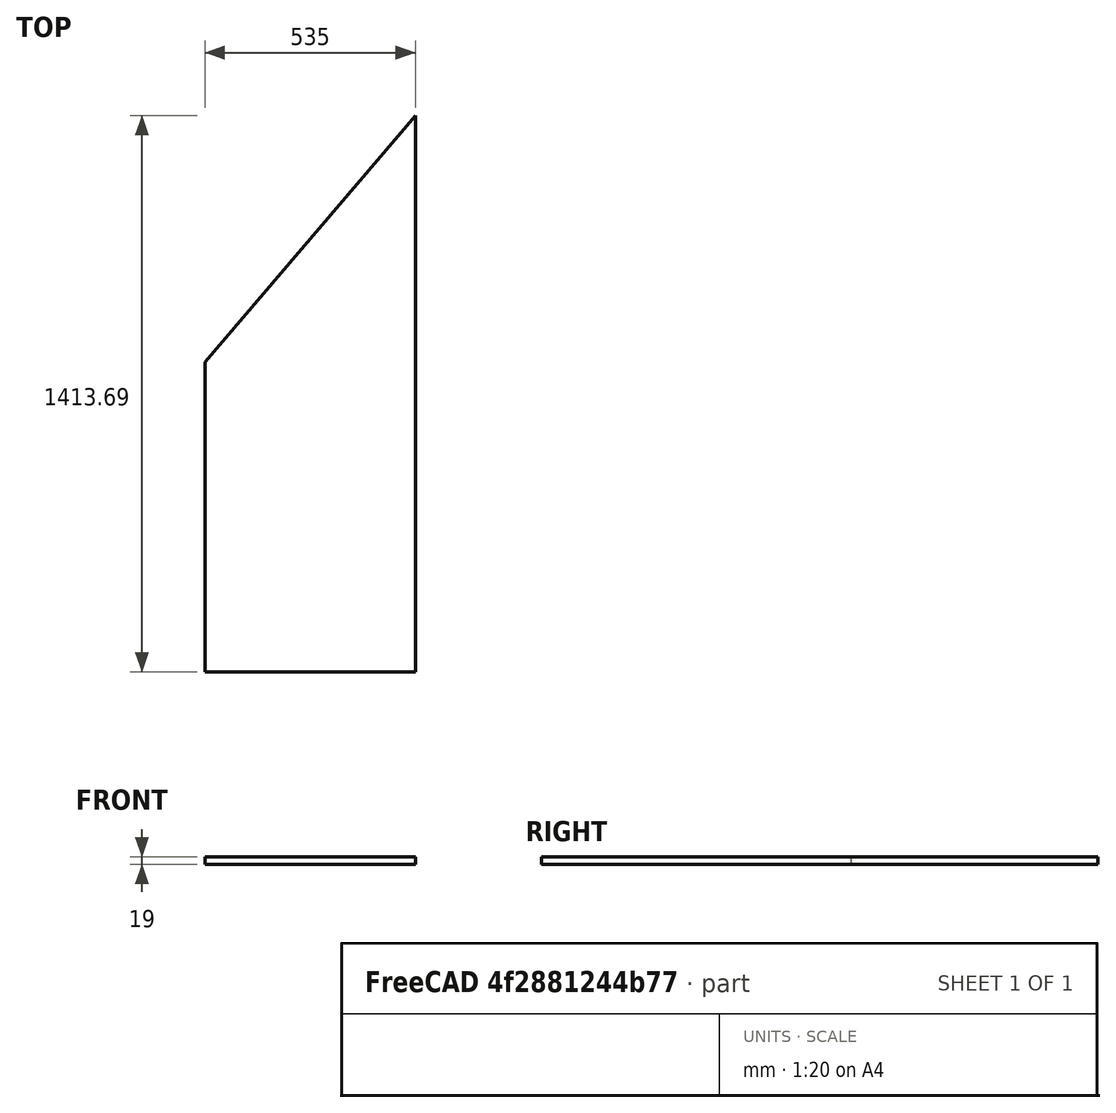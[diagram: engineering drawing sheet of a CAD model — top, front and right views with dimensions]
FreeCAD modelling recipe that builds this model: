
FCSTD DOCUMENT  (FreeCAD 1.0R39285 (Git))
Label: wardrobe_door_corpus02_jan
License: All rights reserved
LicenseURL: https://en.wikipedia.org/wiki/All_rights_reserved
objects: TechDraw::DrawViewDimension×5, PartDesign::CoordinateSystem×2, TechDraw::DrawProjGroupItem×2, Sketcher::SketchObject×1, PartDesign::Pad×1, PartDesign::Body×1, TechDraw::DrawSVGTemplate×1, TechDraw::DrawViewAnnotation×1, TechDraw::DrawPage×1, App::Part×1
note: 15 computed .brp shape members not serialized (recipe doc carries the construction recipe); baked Part::Feature solids carry a one-line shape summary decoded from their .brp
EXTERNAL_REF file=../../mastersheet.FCStd obj=Spreadsheet
EXTERNAL_REF file=../../mastersketch.FCStd obj=Sketch

FEATURE [Sketcher::SketchObject] Sketch
  ArcFitTolerance = 1e-06
  AttachmentSupport = -> [XY_Plane]
  FullyConstrained = true
  MakeInternals = false
  MapMode = 5
  expr: Constraints[0] = mastersketch#Sketch.Constraints.corpus02_door_height
  expr: Constraints[10] = mastersketch#Sketch.Constraints.alpha
  expr: Constraints[3] = mastersheet#Spreadsheet.corpus_width - 5
  sketch-geometry (4):
    g0: LineSegment StartX=0 StartY=0 StartZ=0 EndX=0 EndY=1413.69 EndZ=0
    g1: LineSegment StartX=0 StartY=0 StartZ=0 EndX=-535 EndY=0 EndZ=0
    g2: LineSegment StartX=-535 StartY=0 StartZ=0 EndX=-535 EndY=787.688 EndZ=0
    g3: LineSegment StartX=-535 StartY=787.688 StartZ=0 EndX=0 EndY=1413.69 EndZ=0
  constraints (11):
    c: Distance(g0) = 1413.69
    c: Coincident(g0,g-1)
    c: Vertical(g0)
    c: Distance(g1) = 535
    c: Coincident(g1,g0)
    c: PointOnObject(g1,g-1)
    c: Vertical(g2)
    c: Coincident(g3,g2)
    c: Coincident(g2,g1)
    c: Coincident(g3,g0)
    c: Angle(g2,g3) = 2.43442
FEATURE [PartDesign::Pad] Pad
  Direction = (0,0,1)
  Length = 19
  Length2 = 10
  Profile = -> Sketch
  ReferenceAxis = -> Sketch [N_Axis]
  Refine = true
  Suppressed = false
  Type = 0
FEATURE [PartDesign::Body] Body  label="wardrobe_door_corpus02_jan"
  AllowCompound = false
  Group = -> [Sketch,Pad]
  Origin = -> Origin
  Tip = -> Pad
FEATURE [PartDesign::CoordinateSystem] LCS_1
  AttacherType = Attacher::AttachEngine3D
  AttachmentSupport = -> [Pad]
  MapMode = 7
  Placement = pos=(0,0,0) rot=(1,0,0;1.5708rad)
FEATURE [TechDraw::DrawSVGTemplate] Template  label="Vorlage"
  Height = 210
  Orientation = 1
  Template = <userpath>/scoop/apps/freecad/current/data/Mod/TechDraw/Templates/A4_Landscape_TD.svg
  Width = 297
FEATURE [TechDraw::DrawProjGroupItem] View
  CoarseView = false
  Direction = (0,1e-16,-1)
  Focus = 100
  HardHidden = false
  IsoCount = 0
  IsoHidden = false
  IsoVisible = false
  LockPosition = false
  Perspective = false
  Rotation = 0
  RotationVector = (1,0,0)
  Scale = 0.1
  ScaleType = 2
  ScrubCount = 1
  SeamHidden = false
  SeamVisible = false
  SmoothHidden = false
  SmoothVisible = true
  Source = -> [Body]
  Type = 0
  X = 139.755
  XDirection = (-1e-16,-1,-1e-16)
  Y = 148.199
FEATURE [TechDraw::DrawProjGroupItem] View001
  CoarseView = false
  Direction = (-1,-1e-16,0)
  Focus = 100
  HardHidden = false
  IsoCount = 0
  IsoHidden = false
  IsoVisible = false
  LockPosition = false
  Perspective = false
  Rotation = 0
  RotationVector = (1,0,0)
  Scale = 0.1
  ScaleType = 2
  ScrubCount = 1
  SeamHidden = false
  SeamVisible = false
  SmoothHidden = false
  SmoothVisible = true
  Source = -> [Body]
  Type = 0
  X = 139.755
  XDirection = (1e-16,-1,0)
  Y = 90.1338
FEATURE [TechDraw::DrawViewDimension] Dimension  label="Maß"
  AngleOverride = false
  Arbitrary = false
  ArbitraryTolerances = false
  BoxCorners = (2) [(-70.6847,-26.75,0),(70.6847,26.75,0)]
  EqualTolerance = true
  ExtensionAngle = 0
  FormatSpec = %.1w
  FormatSpecOverTolerance = %+.1w
  FormatSpecUnderTolerance = %+.1w
  Inverted = false
  LineAngle = 0
  LockPosition = false
  MeasureType = 1
  OverTolerance = 0
  References2D = -> [View]
  Rotation = 0
  ScaleType = 0
  TheoreticalExact = false
  Type = 1
  UnderTolerance = 0
  X = 0
  Y = -33.1734
FEATURE [TechDraw::DrawViewDimension] Dimension001  label="Maß001"
  AngleOverride = false
  Arbitrary = false
  ArbitraryTolerances = false
  BoxCorners = (2) [(-70.6847,-26.75,0),(70.6847,26.75,0)]
  EqualTolerance = true
  ExtensionAngle = 0
  FormatSpec = %.1w
  FormatSpecOverTolerance = %+.1w
  FormatSpecUnderTolerance = %+.1w
  Inverted = false
  LineAngle = 0
  LockPosition = false
  MeasureType = 1
  OverTolerance = 0
  References2D = -> [View]
  Rotation = 0
  ScaleType = 0
  TheoreticalExact = false
  Type = 2
  UnderTolerance = 0
  X = 76.0797
  Y = 0
FEATURE [TechDraw::DrawViewDimension] Dimension002  label="Maß002"
  AngleOverride = false
  Arbitrary = false
  ArbitraryTolerances = false
  BoxCorners = (2) [(-70.6847,-26.75,0),(70.6847,26.75,0)]
  EqualTolerance = true
  ExtensionAngle = 0
  FormatSpec = %.1w
  FormatSpecOverTolerance = %+.1w
  FormatSpecUnderTolerance = %+.1w
  Inverted = false
  LineAngle = 0
  LockPosition = false
  MeasureType = 1
  OverTolerance = 0
  References2D = -> [View]
  Rotation = 0
  ScaleType = 0
  TheoreticalExact = false
  Type = 1
  UnderTolerance = 0
  X = 31.3003
  Y = 43.1168
FEATURE [TechDraw::DrawViewDimension] Dimension003  label="Maß003"
  AngleOverride = false
  Arbitrary = false
  ArbitraryTolerances = false
  BoxCorners = (2) [(-70.6847,-0.95,0),(70.6847,0.95,0)]
  EqualTolerance = true
  ExtensionAngle = 0
  FormatSpec = %.1w
  FormatSpecOverTolerance = %+.1w
  FormatSpecUnderTolerance = %+.1w
  Inverted = false
  LineAngle = 0
  LockPosition = false
  MeasureType = 1
  OverTolerance = 0
  References2D = -> [View001]
  Rotation = 0
  ScaleType = 0
  TheoreticalExact = false
  Type = 0
  UnderTolerance = 0
  X = 76.6584
  Y = -13.0761
FEATURE [TechDraw::DrawViewDimension] Dimension004  label="Maß004"
  AngleOverride = false
  Arbitrary = false
  ArbitraryTolerances = false
  BoxCorners = (2) [(-70.6847,-26.75,0),(70.6847,26.75,0)]
  EqualTolerance = true
  ExtensionAngle = 0
  FormatSpec = (%.1w)
  FormatSpecOverTolerance = %+.1w
  FormatSpecUnderTolerance = %+.1w
  Inverted = false
  LineAngle = 0
  LockPosition = false
  MeasureType = 1
  OverTolerance = 0
  References2D = -> [View]
  Rotation = 0
  ScaleType = 0
  TheoreticalExact = false
  Type = 6
  UnderTolerance = 0
  X = -0.468348
  Y = 10.2378
FEATURE [TechDraw::DrawViewAnnotation] Annotation  label="Beschriftung"
  Font = MS Shell Dlg 2
  LineSpace = 100
  LockPosition = false
  MaxWidth = -1
  Rotation = 0
  ScaleType = 0
  Text = Artikelnummer: 12391882 oder 6754673
  TextSize = 5
  TextStyle = 0
  X = 208.828
  Y = 61.9887
FEATURE [TechDraw::DrawPage] Page  label="Seite"
  KeepUpdated = true
  NextBalloonIndex = 1
  ProjectionType = 0
  Template = -> Template
  Views = -> [View,View001,Dimension,Dimension001,Dimension002,Dimension003,Dimension004,Annotation]
FEATURE [PartDesign::CoordinateSystem] LCS_Origin
  AttacherType = Attacher::AttachEngine3D
  AttachmentSupport = -> [X_Axis001]
  MapMode = 2
FEATURE [App::Part] wardrobe_door_corpus02_jan  label="wardrobe_door_corpus02_jan001"
  DrawingName = wardrobe_door_corpus02_jan.FCStd
  Group = -> [LCS_Origin,LCS_1,Body]
  Origin = -> Origin001
  PartDescription = wardrobe_door_corpus02_jan
  PartID = wardrobe_door_corpus02_jan
